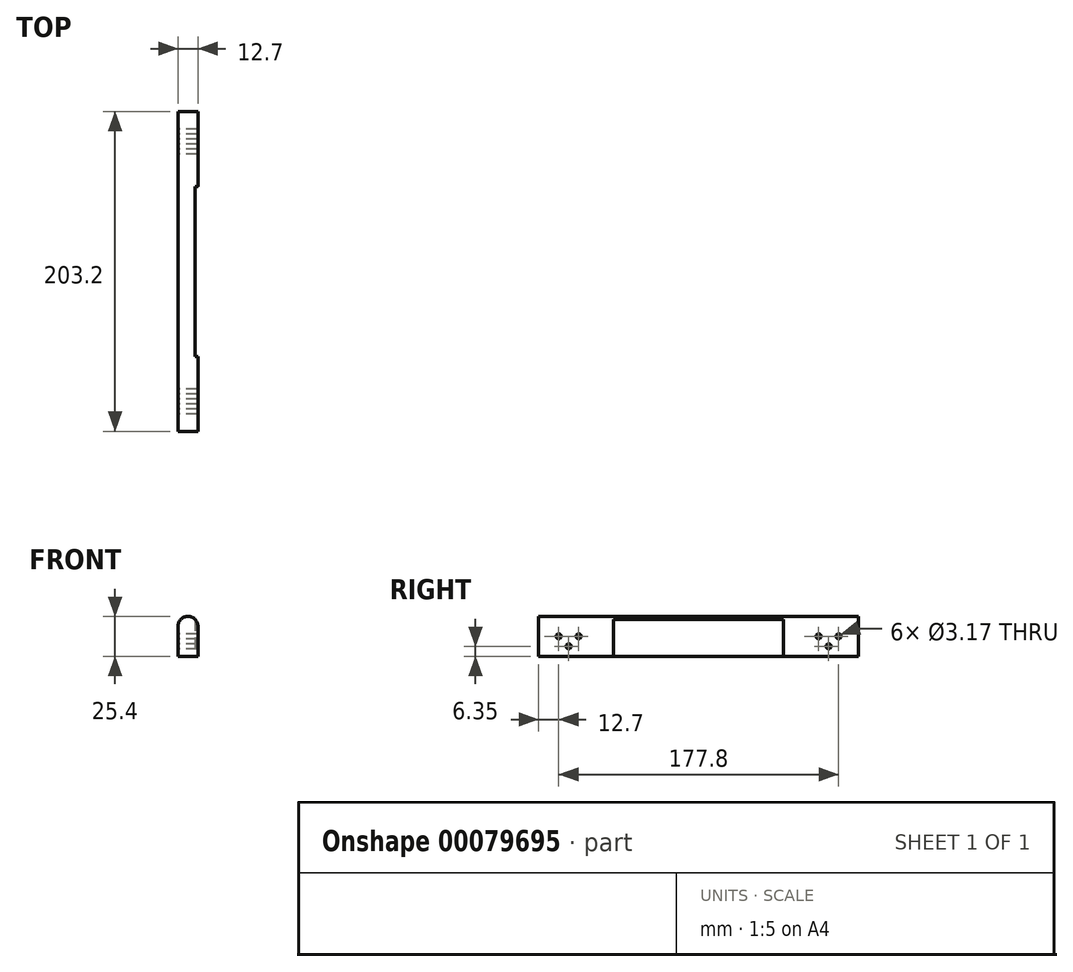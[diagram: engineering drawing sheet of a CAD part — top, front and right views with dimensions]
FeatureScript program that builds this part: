
annotation { "Feature Type Name" : "Feature", "Feature Type Description" : "" }
export const myFeature = defineFeature(function(context is Context, id is Id, definition is map)
    precondition{}
    {
        {
            var Q0;
            Q0=qCreatedBy(makeId("Front.planeOp"),FACE);
            var sketch = newSketch(context, id + "F0", { "sketchPlane" : qUnion([Q0])});
            skLineSegment(sketch, "E0.bottom", {"start": v(6.35, -12.7) * mm, "end": v(-6.35, -12.7) * mm});
            skLineSegment(sketch, "E0.top", {"start": v(6.35, 12.7) * mm, "end": v(-6.35, 12.7) * mm});
            skLineSegment(sketch, "E0.left", {"start": v(6.35, -12.7) * mm, "end": v(6.35, 12.7) * mm});
            skLineSegment(sketch, "E0.right", {"start": v(-6.35, -12.7) * mm, "end": v(-6.35, 12.7) * mm});
            skPoint(sketch, "E0.middle", {"position": v(0, 0) * mm});
            skSolve(sketch);
        }
        {
            var Q0;
            Q0 = qSketchRegion(id + "F0", true);
            extrude(context, id + "F1", {"entities" : qUnion([Q0]), "endBound" : BoundingType.SYMMETRIC, "depth" : 203.2 * mm});
        }
        {
            var Q0;
            Q0=makeQuery(id+"F1.opExtrude","SWEPT_EDGE",EDGE,{"disambiguationData":[OSD([sQuery(id+"F0.wireOp",EDGE,"E0.top"),sQuery(id+"F0.wireOp",EDGE,"E0.right")])]});
            var Q1;
            Q1=makeQuery(id+"F1.opExtrude","SWEPT_EDGE",EDGE,{"disambiguationData":[OSD([sQuery(id+"F0.wireOp",EDGE,"E0.top"),sQuery(id+"F0.wireOp",EDGE,"E0.left")])]});
            fillet(context, id + "F2", {"entities" : qUnion([Q0, Q1]), "radius" : 6.35 * mm, "tangentPropagation" : true, "allowEdgeOverflow" : false});
        }
        {
            var Q0;
            Q0=makeQuery(id+"F1.opExtrude","SWEPT_FACE",FACE,{"disambiguationData":[OSD([sQuery(id+"F0.wireOp",EDGE,"E0.right")])]});
            var sketch = newSketch(context, id + "F3", { "sketchPlane" : qUnion([Q0])});
            skCircle(sketch, "E1", {"center": v(-76.2, 0) * mm, "radius": 1.59 * mm});
            skCircle(sketch, "E2", {"center": v(-88.9, 0) * mm, "radius": 1.59 * mm});
            skCircle(sketch, "E3", {"center": v(76.2, 0) * mm, "radius": 1.59 * mm});
            skCircle(sketch, "E4", {"center": v(88.9, 0) * mm, "radius": 1.59 * mm});
            skPoint(sketch, "E5.endSnap0", {"position": v(82.55, 0) * mm});
            skCircle(sketch, "E6", {"center": v(-82.55, -6.35) * mm, "radius": 1.59 * mm});
            skCircle(sketch, "E7", {"center": v(82.55, -6.35) * mm, "radius": 1.59 * mm});
            skLineSegment(sketch, "E8", {"start": v(0, 0) * mm, "end": v(-88.9, 0) * mm});
            skLineSegment(sketch, "E9", {"start": v(-88.9, 0) * mm, "end": v(88.9, 0) * mm});
            skSolve(sketch);
        }
        {
            var Q0;
            Q0 = qSketchRegion(id + "F3", true);
            extrude(context, id + "F4", {"entities" : qUnion([Q0]), "operationType" : NewBodyOperationType.REMOVE, "oppositeDirection" : true, "depth" : 25.4 * mm});
        }
        {
            var Q0;
            Q0=makeQuery(id+"F1.opExtrude","SWEPT_FACE",FACE,{"disambiguationData":[OSD([sQuery(id+"F0.wireOp",EDGE,"E0.bottom")])]});
            var sketch = newSketch(context, id + "F5", { "sketchPlane" : qUnion([Q0])});
            skLineSegment(sketch, "E10.bottom", {"start": v(4.45, 53.98) * mm, "end": v(8.26, 53.98) * mm});
            skLineSegment(sketch, "E10.top", {"start": v(4.45, -53.98) * mm, "end": v(8.26, -53.98) * mm});
            skLineSegment(sketch, "E10.left", {"start": v(4.45, 53.98) * mm, "end": v(4.45, -53.98) * mm});
            skLineSegment(sketch, "E10.right", {"start": v(8.26, 53.98) * mm, "end": v(8.26, -53.98) * mm});
            skPoint(sketch, "E10.middle", {"position": v(6.35, 0) * mm});
            skSolve(sketch);
        }
        {
            var Q0;
            Q0 = qSketchRegion(id + "F5", true);
            extrude(context, id + "F6", {"entities" : qUnion([Q0]), "operationType" : NewBodyOperationType.REMOVE, "oppositeDirection" : true, "depth" : 25.4 * mm});
        }
    });
